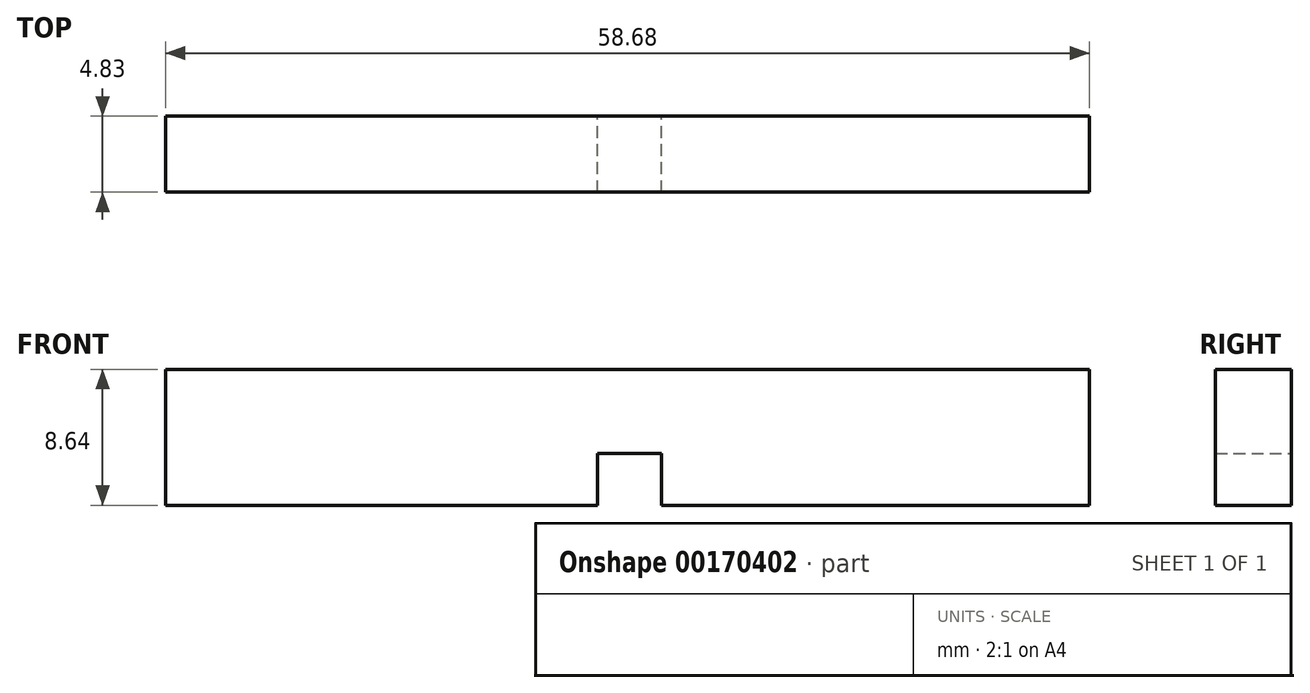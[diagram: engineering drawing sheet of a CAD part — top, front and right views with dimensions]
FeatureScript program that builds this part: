
annotation { "Feature Type Name" : "Feature", "Feature Type Description" : "" }
export const myFeature = defineFeature(function(context is Context, id is Id, definition is map)
    precondition{}
    {
        {
            var Q0;
            Q0=qCreatedBy(makeId("Front.planeOp"),FACE);
            var sketch = newSketch(context, id + "F0", { "sketchPlane" : qUnion([Q0])});
            skLineSegment(sketch, "E0.bottom", {"start": v(-29.34, 4.32) * mm, "end": v(29.34, 4.32) * mm});
            skLineSegment(sketch, "E0.top", {"start": v(-29.34, -4.32) * mm, "end": v(-1.9, -4.32) * mm});
            skLineSegment(sketch, "E0.left", {"start": v(-29.34, 4.32) * mm, "end": v(-29.34, -4.32) * mm});
            skLineSegment(sketch, "E0.right", {"start": v(29.34, 4.32) * mm, "end": v(29.34, -4.32) * mm});
            skLineSegment(sketch, "E1.bottom", {"start": v(-1.9, -1.02) * mm, "end": v(2.16, -1.02) * mm});
            skLineSegment(sketch, "E1.left", {"start": v(-1.9, -1.02) * mm, "end": v(-1.9, -4.32) * mm});
            skLineSegment(sketch, "E1.right", {"start": v(2.16, -1.02) * mm, "end": v(2.16, -4.32) * mm});
            skLineSegment(sketch, "E2.trimOffspring", {"start": v(2.16, -4.32) * mm, "end": v(29.34, -4.32) * mm});
            skPoint(sketch, "E1.top.end.orphan", {"position": v(2.16, -9.45) * mm});
            skPoint(sketch, "E3.orphan", {"position": v(-1.9, -9.45) * mm});
            skSolve(sketch);
        }
        {
            var Q0;
            Q0 = qSketchRegion(id + "F0", true);
            extrude(context, id + "F1", {"entities" : qUnion([Q0]), "depth" : 4.83 * mm});
        }
    });
